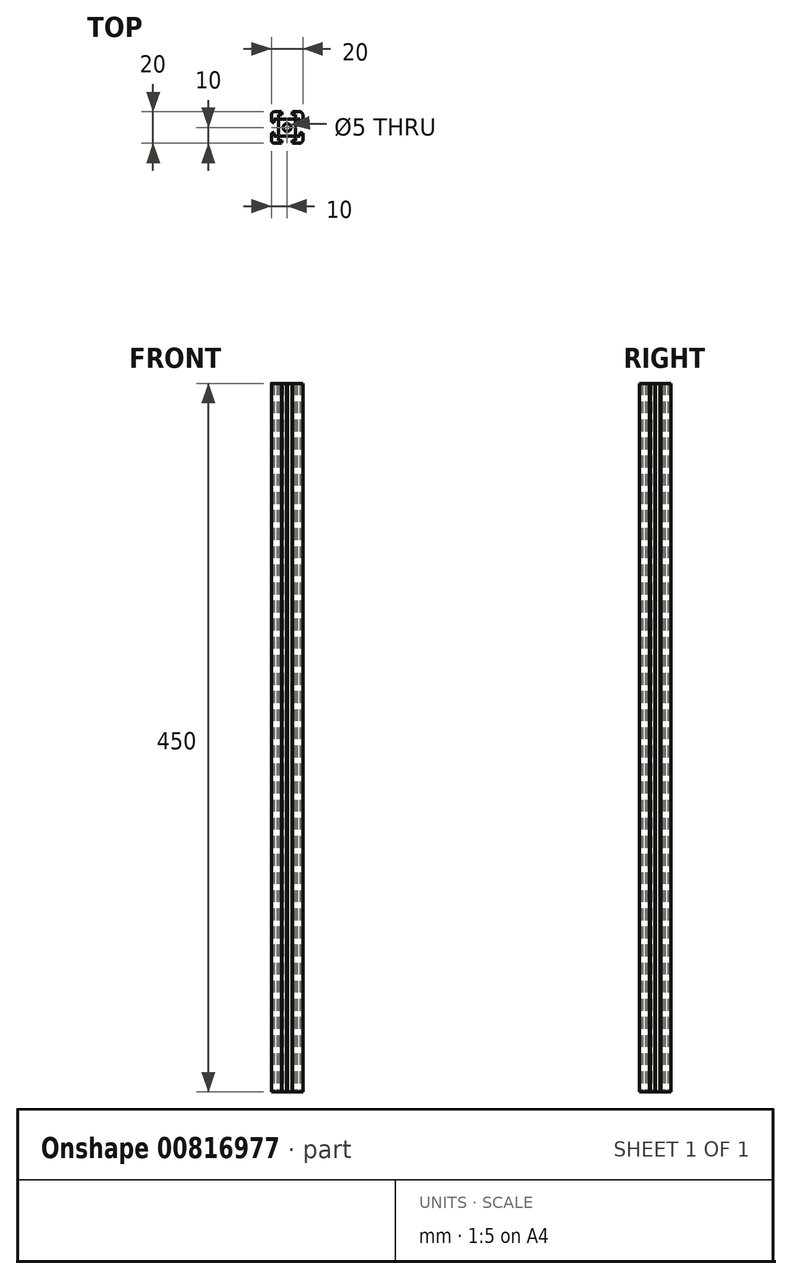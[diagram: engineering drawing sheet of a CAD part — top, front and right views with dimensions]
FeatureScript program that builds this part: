
annotation { "Feature Type Name" : "Feature", "Feature Type Description" : "" }
export const myFeature = defineFeature(function(context is Context, id is Id, definition is map)
    precondition{}
    {
        {
            var Q0;
            Q0=qCreatedBy(makeId("Top.planeOp"),FACE);
            var sketch = newSketch(context, id + "F0", { "sketchPlane" : qUnion([Q0])});
            skLineSegment(sketch, "E0.bottom", {"start": v(8, 10) * mm, "end": v(3.6, 10) * mm});
            skPoint(sketch, "E0.middle", {"position": v(0, 0) * mm});
            skLineSegment(sketch, "E1.bottom", {"start": v(4.58, 5.43) * mm, "end": v(0.25, 5.43) * mm});
            skLineSegment(sketch, "E2", {"start": v(-10, 10) * mm, "end": v(10, -10) * mm, "construction": true});
            skLineSegment(sketch, "E3", {"start": v(10, 10) * mm, "end": v(-10, -10) * mm, "construction": true});
            skLineSegment(sketch, "E4", {"start": v(-3.6, 10) * mm, "end": v(-3.6, 9.1) * mm});
            skLineSegment(sketch, "E5", {"start": v(-3.6, 9.1) * mm, "end": v(-3.1, 9.1) * mm});
            skLineSegment(sketch, "E6", {"start": v(-3.1, 9.1) * mm, "end": v(-3.1, 8.2) * mm});
            skLineSegment(sketch, "E7", {"start": v(-3.1, 8.2) * mm, "end": v(-5.45, 8.2) * mm});
            skLineSegment(sketch, "E8", {"start": v(-5.45, 8.2) * mm, "end": v(-5.45, 6.3) * mm});
            skLineSegment(sketch, "E9", {"start": v(-5.45, 6.3) * mm, "end": v(-4.58, 5.43) * mm});
            skLineSegment(sketch, "E10.MirrorCS", {"start": v(5.45, 8.2) * mm, "end": v(5.45, 6.3) * mm});
            skLineSegment(sketch, "E11.MirrorCS", {"start": v(3.1, 9.1) * mm, "end": v(3.1, 8.2) * mm});
            skLineSegment(sketch, "E12.MirrorCS", {"start": v(3.6, 10) * mm, "end": v(3.6, 9.1) * mm});
            skLineSegment(sketch, "E13.MirrorCS", {"start": v(3.1, 8.2) * mm, "end": v(5.45, 8.2) * mm});
            skLineSegment(sketch, "E14.MirrorCS", {"start": v(3.6, 9.1) * mm, "end": v(3.1, 9.1) * mm});
            skLineSegment(sketch, "E15.MirrorCS", {"start": v(5.45, 6.3) * mm, "end": v(4.58, 5.43) * mm});
            skPoint(sketch, "E16.visualSharp", {"position": v(-10, 10) * mm});
            skPoint(sketch, "E17.visualSharp", {"position": v(10, 10) * mm});
            skLineSegment(sketch, "E18.trimOffspring", {"start": v(-3.6, 10) * mm, "end": v(-8, 10) * mm});
            skLineSegment(sketch, "E19.1.0", {"start": v(-8.2, -3.1) * mm, "end": v(-8.2, -5.45) * mm});
            skLineSegment(sketch, "E19.1.2", {"start": v(-8.2, 5.45) * mm, "end": v(-6.3, 5.45) * mm});
            skLineSegment(sketch, "E19.1.3", {"start": v(-8.2, 3.1) * mm, "end": v(-8.2, 5.45) * mm});
            skPoint(sketch, "E19.1.4", {"position": v(-10, -10) * mm});
            skLineSegment(sketch, "E19.1.5", {"start": v(-9.1, -3.1) * mm, "end": v(-8.2, -3.1) * mm});
            skLineSegment(sketch, "E19.1.6", {"start": v(-6.3, 5.45) * mm, "end": v(-5.43, 4.58) * mm});
            skLineSegment(sketch, "E19.1.7", {"start": v(-5.43, 4.58) * mm, "end": v(-5.43, 0.25) * mm});
            skLineSegment(sketch, "E19.1.8", {"start": v(-8.2, -5.45) * mm, "end": v(-6.3, -5.45) * mm});
            skLineSegment(sketch, "E19.1.9", {"start": v(-9.1, 3.1) * mm, "end": v(-8.2, 3.1) * mm});
            skLineSegment(sketch, "E19.1.10", {"start": v(-6.3, -5.45) * mm, "end": v(-5.43, -4.58) * mm});
            skLineSegment(sketch, "E19.1.11", {"start": v(-10, 8) * mm, "end": v(-10, 3.6) * mm});
            skLineSegment(sketch, "E19.1.12", {"start": v(-10, -3.6) * mm, "end": v(-10, -8) * mm});
            skLineSegment(sketch, "E19.1.13", {"start": v(-10, 3.6) * mm, "end": v(-9.1, 3.6) * mm});
            skLineSegment(sketch, "E19.1.14", {"start": v(-9.1, -3.6) * mm, "end": v(-9.1, -3.1) * mm});
            skLineSegment(sketch, "E19.1.15", {"start": v(-10, -3.6) * mm, "end": v(-9.1, -3.6) * mm});
            skLineSegment(sketch, "E19.1.16", {"start": v(-9.1, 3.6) * mm, "end": v(-9.1, 3.1) * mm});
            skLineSegment(sketch, "E19.2.0", {"start": v(3.1, -8.2) * mm, "end": v(5.45, -8.2) * mm});
            skPoint(sketch, "E19.2.1", {"position": v(-10, -10) * mm});
            skLineSegment(sketch, "E19.2.2", {"start": v(-5.45, -8.2) * mm, "end": v(-5.45, -6.3) * mm});
            skLineSegment(sketch, "E19.2.3", {"start": v(-3.1, -8.2) * mm, "end": v(-5.45, -8.2) * mm});
            skPoint(sketch, "E19.2.4", {"position": v(10, -10) * mm});
            skLineSegment(sketch, "E19.2.5", {"start": v(3.1, -9.1) * mm, "end": v(3.1, -8.2) * mm});
            skLineSegment(sketch, "E19.2.6", {"start": v(-5.45, -6.3) * mm, "end": v(-4.58, -5.43) * mm});
            skLineSegment(sketch, "E19.2.7", {"start": v(-4.58, -5.43) * mm, "end": v(-0.25, -5.43) * mm});
            skLineSegment(sketch, "E19.2.8", {"start": v(5.45, -8.2) * mm, "end": v(5.45, -6.3) * mm});
            skLineSegment(sketch, "E19.2.9", {"start": v(-3.1, -9.1) * mm, "end": v(-3.1, -8.2) * mm});
            skLineSegment(sketch, "E19.2.10", {"start": v(5.45, -6.3) * mm, "end": v(4.58, -5.43) * mm});
            skLineSegment(sketch, "E19.2.11", {"start": v(-8, -10) * mm, "end": v(-3.6, -10) * mm});
            skLineSegment(sketch, "E19.2.12", {"start": v(3.6, -10) * mm, "end": v(8, -10) * mm});
            skLineSegment(sketch, "E19.2.13", {"start": v(-3.6, -10) * mm, "end": v(-3.6, -9.1) * mm});
            skLineSegment(sketch, "E19.2.14", {"start": v(3.6, -9.1) * mm, "end": v(3.1, -9.1) * mm});
            skLineSegment(sketch, "E19.2.15", {"start": v(3.6, -10) * mm, "end": v(3.6, -9.1) * mm});
            skLineSegment(sketch, "E19.2.16", {"start": v(-3.6, -9.1) * mm, "end": v(-3.1, -9.1) * mm});
            skLineSegment(sketch, "E19.3.0", {"start": v(8.2, 3.1) * mm, "end": v(8.2, 5.45) * mm});
            skPoint(sketch, "E19.3.1", {"position": v(10, -10) * mm});
            skLineSegment(sketch, "E19.3.2", {"start": v(8.2, -5.45) * mm, "end": v(6.3, -5.45) * mm});
            skLineSegment(sketch, "E19.3.3", {"start": v(8.2, -3.1) * mm, "end": v(8.2, -5.45) * mm});
            skLineSegment(sketch, "E19.3.5", {"start": v(9.1, 3.1) * mm, "end": v(8.2, 3.1) * mm});
            skLineSegment(sketch, "E19.3.6", {"start": v(6.3, -5.45) * mm, "end": v(5.43, -4.58) * mm});
            skLineSegment(sketch, "E19.3.7", {"start": v(5.43, -4.58) * mm, "end": v(5.43, -0.25) * mm});
            skLineSegment(sketch, "E19.3.8", {"start": v(8.2, 5.45) * mm, "end": v(6.3, 5.45) * mm});
            skLineSegment(sketch, "E19.3.9", {"start": v(9.1, -3.1) * mm, "end": v(8.2, -3.1) * mm});
            skLineSegment(sketch, "E19.3.10", {"start": v(6.3, 5.45) * mm, "end": v(5.43, 4.58) * mm});
            skLineSegment(sketch, "E19.3.11", {"start": v(10, -8) * mm, "end": v(10, -3.6) * mm});
            skLineSegment(sketch, "E19.3.12", {"start": v(10, 3.6) * mm, "end": v(10, 8) * mm});
            skLineSegment(sketch, "E19.3.13", {"start": v(10, -3.6) * mm, "end": v(9.1, -3.6) * mm});
            skLineSegment(sketch, "E19.3.14", {"start": v(9.1, 3.6) * mm, "end": v(9.1, 3.1) * mm});
            skLineSegment(sketch, "E19.3.15", {"start": v(10, 3.6) * mm, "end": v(9.1, 3.6) * mm});
            skLineSegment(sketch, "E19.3.16", {"start": v(9.1, -3.6) * mm, "end": v(9.1, -3.1) * mm});
            skCircle(sketch, "E20", {"center": v(0, 0) * mm, "radius": 2.5 * mm});
            skLineSegment(sketch, "E21", {"start": v(-0.25, 5.43) * mm, "end": v(0, 4.93) * mm});
            skLineSegment(sketch, "E22", {"start": v(0, 4.93) * mm, "end": v(0.25, 5.43) * mm});
            skLineSegment(sketch, "E23.trimOffspring", {"start": v(-0.25, 5.43) * mm, "end": v(-4.58, 5.43) * mm});
            skLineSegment(sketch, "E24.1.0", {"start": v(-4.93, 0) * mm, "end": v(-5.43, 0.25) * mm});
            skLineSegment(sketch, "E24.1.1", {"start": v(-5.43, -0.25) * mm, "end": v(-4.93, 0) * mm});
            skLineSegment(sketch, "E24.2.0", {"start": v(0, -4.93) * mm, "end": v(-0.25, -5.43) * mm});
            skLineSegment(sketch, "E24.2.1", {"start": v(0.25, -5.43) * mm, "end": v(0, -4.93) * mm});
            skLineSegment(sketch, "E24.3.0", {"start": v(4.93, 0) * mm, "end": v(5.43, -0.25) * mm});
            skLineSegment(sketch, "E24.3.1", {"start": v(5.43, 0.25) * mm, "end": v(4.93, 0) * mm});
            skLineSegment(sketch, "E25.trimOffspring", {"start": v(5.43, 0.25) * mm, "end": v(5.43, 4.58) * mm});
            skLineSegment(sketch, "E26.trimOffspring", {"start": v(0.25, -5.43) * mm, "end": v(4.58, -5.43) * mm});
            skLineSegment(sketch, "E27.trimOffspring", {"start": v(-5.43, -0.25) * mm, "end": v(-5.43, -4.58) * mm});
            skArc(sketch, "E28.filletArc", {"start": v(10, 8) * mm, "mid": v(9.41, 9.41) * mm, "end": v(8, 10) * mm});
            skArc(sketch, "E29.filletArc", {"start": v(8, -10) * mm, "mid": v(9.41, -9.41) * mm, "end": v(10, -8) * mm});
            skArc(sketch, "E30.filletArc", {"start": v(-10, -8) * mm, "mid": v(-9.41, -9.41) * mm, "end": v(-8, -10) * mm});
            skArc(sketch, "E31.filletArc", {"start": v(-8, 10) * mm, "mid": v(-9.41, 9.41) * mm, "end": v(-10, 8) * mm});
            skSolve(sketch);
        }
        {
            var Q0;
            Q0=makeQuery(id+"F0.imprint","IMPRINT",FACE,{"disambiguationData":[TD([[makeQuery(id+"F0.imprint","IMPRINT",EDGE,{"derivedFrom":sQuery(id+"F0.wireOp",EDGE,"E0.bottom")}),1.0]])]});
            extrude(context, id + "F1", {"entities" : qUnion([Q0]), "depth" : 450 * mm, "offsetDistance" : 25 * mm});
        }
    });
